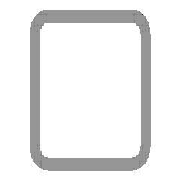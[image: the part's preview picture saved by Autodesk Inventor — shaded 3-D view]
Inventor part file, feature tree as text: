
AUTODESK INVENTOR PART (.ipt)
format: ipt  version: 2023.1 (Build 271208000, 208)  size: 148,992 bytes
history: native  units: mm (DEFAULTED — no unit token found)
features: other x4, plane x3, sketch x3, split x2
ambient origin geometry x8: Origin, YZ Plane, XZ Plane, XY Plane, X Axis, Y Axis, Z Axis, Center Point
bodies: Solid1 (feature_tree), Body (feature_tree)
feature tree (12):
  parser-record x1  (decoder bookkeeping rows leaked as tree rows — omitted from the tree; the rows remain in map.json)
  other  "Driven Length"
  other  "Start Plane"
  other  "End Plane"
  plane  "Work Plane4"
  split  "Split1"
  plane  "Work Plane5"
  split  "Split2"
  sketch  "Sketch"  dims[d10=50.8mm d11=50.8mm d12=3.175mm d13=-25.4mm d14=533.4mm d15=25.4mm d16=25.4mm d17=6.35mm d18=90.0deg d19=558.8mm]
  sketch  "Sketch3"  dims[d3=558.8mm]
  plane  "Work Plane3"
  sketch  "Sketch4"  dims[d4=0.0mm]
